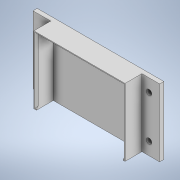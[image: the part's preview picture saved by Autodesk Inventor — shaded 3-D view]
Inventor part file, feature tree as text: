
AUTODESK INVENTOR PART (.ipt)
format: ipt  version: 2020 (Build 240168000, 168)  size: 172,032 bytes
history: native  units: in
note: dims shown in document units (in); Inventor stores cm internally (conversion verified against a paired STEP export)
features: extrude x4, sketch x4, chamfer x3, fillet x2
ambient origin geometry x8: Origin, YZ Plane, XZ Plane, XY Plane, X Axis, Y Axis, Z Axis, Center Point
bodies: Solid1 (feature_tree)
feature tree (13):
  extrude  "Extrusion1"  Depth=3.1496in
  extrude  "Extrusion2"  Depth=4.252in
  chamfer  "Chamfer1"  Distance=0.1181in
  chamfer  "Chamfer2"  Distance=0.1181in
  chamfer  "Chamfer3"  Distance=0.8268in
  extrude  "Extrusion3"  Depth=0.7874in TaperAngle=0.0deg
  extrude  "Extrusion5"  Depth=0.0787in TaperAngle=45.0deg
  fillet  "Fillet1"  Radius=0.0787in
  fillet  "Fillet2"  Radius=0.0787in
  sketch  "Sketch1"  dims[d0=5.9055in d1=3.1496in]
  sketch  "Sketch2"  dims[d2=0.1969in d3=0.0in d4=4.252in]
  sketch  "Sketch3"  dims[d5=4.0157in]
  sketch  "Sketch4"  dims[d6=0.1181in d7=0.1181in d8=0.1181in d9=0.8268in d10=0.7874in d11=0.0in d12=0.0787in d13=0.0787in d14=45.0deg d15=0.0787in d16=0.0787in d17=45.0deg d18=0.0787in d19=0.0787in d20=45.0deg d21=0.2559in d22=0.2559in d23=0.4921in d24=0.4921in d25=1.9685in d26=0.5906in d27=2.9528in d28=2.3622in d29=0.0in d32=0.3937in d33=0.0in d34=0.0787in d35=0.0394in]
